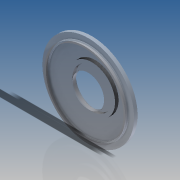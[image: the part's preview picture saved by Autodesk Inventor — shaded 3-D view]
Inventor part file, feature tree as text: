
AUTODESK INVENTOR PART (.ipt)
format: ipt  version: 2016 SP2 (Build 200236200, 236)  size: 146,432 bytes
history: native  units: in
note: dims shown in document units (in); Inventor stores cm internally (conversion verified against a paired STEP export)
features: revolve x1, sketch x1
ambient origin geometry x8: Origin, YZ Plane, XZ Plane, XY Plane, X Axis, Y Axis, Z Axis, Center Point
bodies: Solid1 (feature_tree)
feature tree (2):
  revolve  "Revolution1"  [1 undecoded]
  sketch  "Sketch2"  dims[d0=0.3465in d1=0.4157in d2=0.0315in d3=0.8189in d5=0.0315in d6=0.2835in d7=0.7244in d8=0.6929in d9=0.0315in d10=90.0deg]
note: 1 required parameter value undecoded (feature->parameter linkage not recoverable at this tier; creation-order binding heuristic only, values carry confidence <= 0.55)
